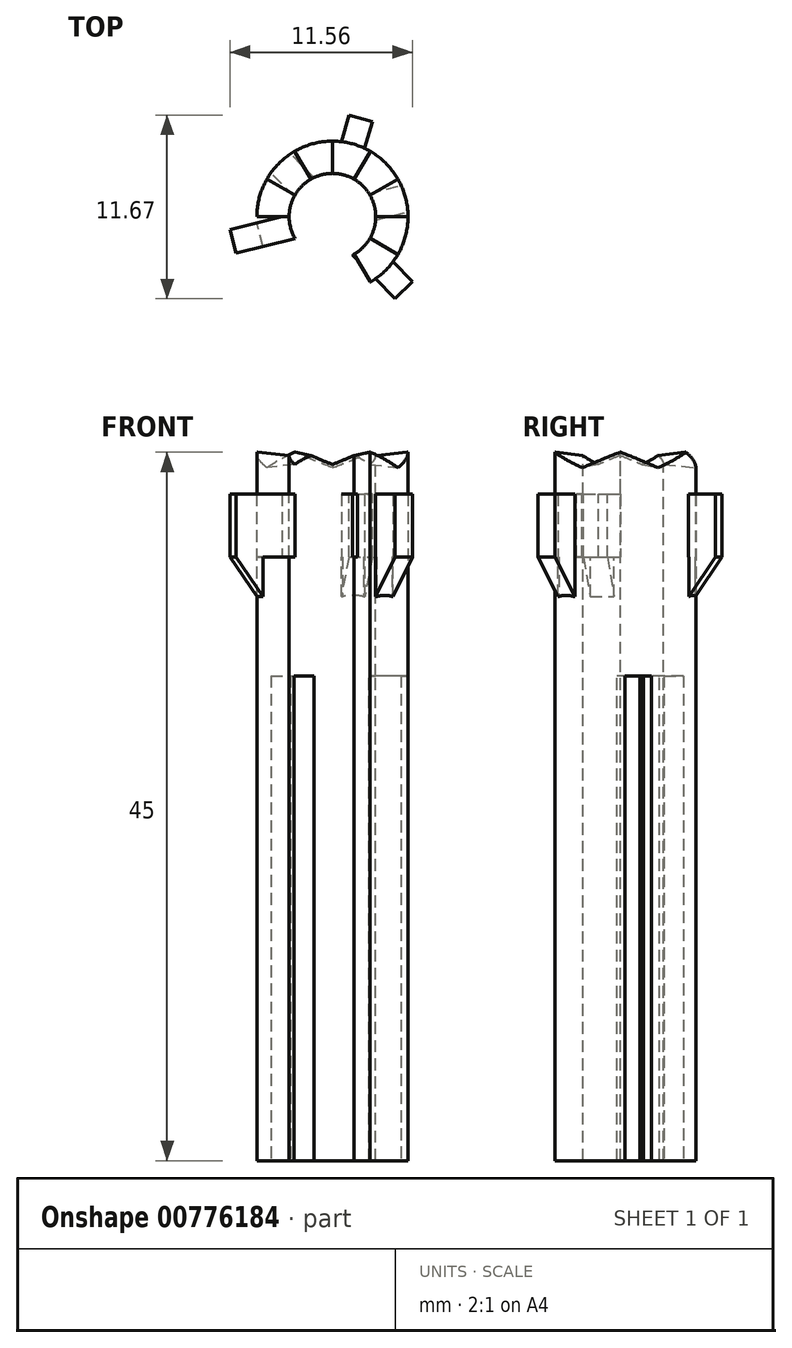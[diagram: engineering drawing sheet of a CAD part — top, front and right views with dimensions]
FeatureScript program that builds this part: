
annotation { "Feature Type Name" : "Feature", "Feature Type Description" : "" }
export const myFeature = defineFeature(function(context is Context, id is Id, definition is map)
    precondition{}
    {
        {
            var Q0;
            Q0=qCreatedBy(makeId("Front.planeOp"),FACE);
            var sketch = newSketch(context, id + "F0", { "sketchPlane" : qUnion([Q0])});
            skLineSegment(sketch, "E0.bottom", {"start": v(0, 0) * mm, "end": v(4.8, 0) * mm});
            skLineSegment(sketch, "E0.top", {"start": v(0, 45) * mm, "end": v(4.8, 45) * mm});
            skLineSegment(sketch, "E0.left", {"start": v(0, 0) * mm, "end": v(0, 45) * mm});
            skLineSegment(sketch, "E0.right", {"start": v(4.8, 0) * mm, "end": v(4.8, 45) * mm});
            skPoint(sketch, "E0.middle", {"position": v(2.4, 22.5) * mm});
            skSolve(sketch);
        }
        {
            var Q0;
            Q0=makeQuery(id+"F0.imprint","IMPRINT",FACE,{"disambiguationData":[TD([[makeQuery(id+"F0.imprint","IMPRINT",EDGE,{"derivedFrom":sQuery(id+"F0.wireOp",EDGE,"E0.bottom")}),1.0]])]});
            var Q1;
            Q1=sQuery(id+"F0.wireOp",EDGE,"E0.left");
            revolve(context, id + "F1", {"surfaceOperationType" : NewSurfaceOperationType.NEW, "entities" : qUnion([Q0]), "axis" : qUnion([Q1]), "revolveType" : RevolveType.ONE_DIRECTION, "angle" : 30 * degree});
        }
        {
            var Q0;
            Q0=sQuery(id+"F0.wireOp",EDGE,"E0.left");
            cPlane(context, id + "F2", {"entities" : qUnion([Q0]), "cplaneType" : CPlaneType.LINE_ANGLE, "offset" : 25 * mm, "angle" : 15 * degree, "width" : 150 * mm, "height" : 150 * mm});
        }
        {
            var Q0;
            Q0=qCreatedBy(id+"F2.planeOp",FACE);
            var sketch = newSketch(context, id + "F3", { "sketchPlane" : qUnion([Q0])});
            skLineSegment(sketch, "E1", {"start": v(0, 45.1) * mm, "end": v(1.34, 45.1) * mm});
            skLineSegment(sketch, "E2", {"start": v(1.34, 45.1) * mm, "end": v(1.34, 43.97) * mm});
            skLineSegment(sketch, "E3", {"start": v(1.34, 43.97) * mm, "end": v(-1.47, 45.1) * mm});
            skLineSegment(sketch, "E4", {"start": v(-1.47, 45.1) * mm, "end": v(0, 45.1) * mm});
            skSolve(sketch);
        }
        {
            var Q0;
            Q0=makeQuery(id+"F3.imprint","IMPRINT",FACE,{"disambiguationData":[TD([[makeQuery(id+"F3.imprint","IMPRINT",EDGE,{"derivedFrom":sQuery(id+"F3.wireOp",EDGE,"E1")}),-1.0]])]});
            extrude(context, id + "F4", {"entities" : qUnion([Q0]), "operationType" : NewBodyOperationType.REMOVE, "depth" : 5.8 * mm, "offsetDistance" : 25 * mm});
        }
        {
            var Q0;
            Q0=makeQuery(id+"F14.boolean.opBoolean","SPLIT",BODY,{"disambiguationData":[OD(0.0)],"derivedFrom":makeQuery(id+"F1.opRevolve","SWEPT_BODY",BODY,{"disambiguationData":[OSD([sQuery(id+"F0.wireOp",EDGE,"E0.bottom"),sQuery(id+"F0.wireOp",EDGE,"E0.top"),sQuery(id+"F0.wireOp",EDGE,"E0.left"),sQuery(id+"F0.wireOp",EDGE,"E0.right")])]})});
            var Q1;
            Q1=makeQuery(id+"F1.opRevolve","CAP_FACE",FACE,{"disambiguationData":[OSD([sQuery(id+"F0.wireOp",EDGE,"E0.bottom"),sQuery(id+"F0.wireOp",EDGE,"E0.top"),sQuery(id+"F0.wireOp",EDGE,"E0.left"),sQuery(id+"F0.wireOp",EDGE,"E0.right")])],"isStart":false});
            mirror(context, id + "F5", {"operationType" : NewBodyOperationType.ADD, "entities" : qUnion([Q0]), "mirrorPlane" : qUnion([Q1])});
        }
        {
            var Q0;
            Q0=makeQuery(id+"F14.boolean.opBoolean","SPLIT",BODY,{"disambiguationData":[OD(0.0)],"derivedFrom":makeQuery(id+"F1.opRevolve","SWEPT_BODY",BODY,{"disambiguationData":[OSD([sQuery(id+"F0.wireOp",EDGE,"E0.bottom"),sQuery(id+"F0.wireOp",EDGE,"E0.top"),sQuery(id+"F0.wireOp",EDGE,"E0.left"),sQuery(id+"F0.wireOp",EDGE,"E0.right")])]})});
            var Q1;
            Q1=makeQuery(id+"F5.opPattern","COPY",FACE,{"derivedFrom":makeQuery(id+"F1.opRevolve","CAP_FACE",FACE,{"disambiguationData":[OSD([sQuery(id+"F0.wireOp",EDGE,"E0.bottom"),sQuery(id+"F0.wireOp",EDGE,"E0.top"),sQuery(id+"F0.wireOp",EDGE,"E0.left"),sQuery(id+"F0.wireOp",EDGE,"E0.right")])],"isStart":true}),"instanceName":"1"});
            mirror(context, id + "F6", {"entities" : qUnion([Q0]), "mirrorPlane" : qUnion([Q1])});
        }
        {
            var Q0;
            Q0=makeQuery(id+"F6.opPattern","COPY",BODY,{"derivedFrom":makeQuery(id+"F14.boolean.opBoolean","SPLIT",BODY,{"disambiguationData":[OD(0.0)],"derivedFrom":makeQuery(id+"F1.opRevolve","SWEPT_BODY",BODY,{"disambiguationData":[OSD([sQuery(id+"F0.wireOp",EDGE,"E0.bottom"),sQuery(id+"F0.wireOp",EDGE,"E0.top"),sQuery(id+"F0.wireOp",EDGE,"E0.left"),sQuery(id+"F0.wireOp",EDGE,"E0.right")])]})}),"instanceName":"1"});
            var Q1;
            Q1=makeQuery(id+"F6.opPattern","COPY",FACE,{"derivedFrom":makeQuery(id+"F1.opRevolve","CAP_FACE",FACE,{"disambiguationData":[OSD([sQuery(id+"F0.wireOp",EDGE,"E0.bottom"),sQuery(id+"F0.wireOp",EDGE,"E0.top"),sQuery(id+"F0.wireOp",EDGE,"E0.left"),sQuery(id+"F0.wireOp",EDGE,"E0.right")])],"isStart":true}),"instanceName":"1"});
            mirror(context, id + "F7", {"entities" : qUnion([Q0]), "mirrorPlane" : qUnion([Q1])});
        }
        {
            var Q0;
            Q0=makeQuery(id+"F14.boolean.opBoolean","SPLIT",BODY,{"disambiguationData":[OD(0.0)],"derivedFrom":makeQuery(id+"F1.opRevolve","SWEPT_BODY",BODY,{"disambiguationData":[OSD([sQuery(id+"F0.wireOp",EDGE,"E0.bottom"),sQuery(id+"F0.wireOp",EDGE,"E0.top"),sQuery(id+"F0.wireOp",EDGE,"E0.left"),sQuery(id+"F0.wireOp",EDGE,"E0.right")])]})});
            var Q1;
            Q1=makeQuery(id+"F7.opPattern","COPY",FACE,{"derivedFrom":makeQuery(id+"F6.opPattern","COPY",FACE,{"derivedFrom":makeQuery(id+"F5.opPattern","COPY",FACE,{"derivedFrom":makeQuery(id+"F1.opRevolve","CAP_FACE",FACE,{"disambiguationData":[OSD([sQuery(id+"F0.wireOp",EDGE,"E0.bottom"),sQuery(id+"F0.wireOp",EDGE,"E0.top"),sQuery(id+"F0.wireOp",EDGE,"E0.left"),sQuery(id+"F0.wireOp",EDGE,"E0.right")])],"isStart":true}),"instanceName":"1"}),"instanceName":"1"}),"instanceName":"1"});
            mirror(context, id + "F8", {"operationType" : NewBodyOperationType.ADD, "entities" : qUnion([Q0]), "mirrorPlane" : qUnion([Q1])});
        }
        {
            var Q0;
            Q0=qCreatedBy(makeId("Right.planeOp"),FACE);
            var sketch = newSketch(context, id + "F9", { "sketchPlane" : qUnion([Q0])});
            skLineSegment(sketch, "E5.bottom", {"start": v(0, 0) * mm, "end": v(2.75, 0) * mm});
            skLineSegment(sketch, "E5.top", {"start": v(0, 45) * mm, "end": v(2.75, 45) * mm});
            skLineSegment(sketch, "E5.left", {"start": v(0, 0) * mm, "end": v(0, 45) * mm});
            skLineSegment(sketch, "E5.right", {"start": v(2.75, 0) * mm, "end": v(2.75, 45) * mm});
            skPoint(sketch, "E5.middle", {"position": v(1.37, 22.5) * mm});
            skSolve(sketch);
        }
        {
            var Q0;
            Q0=sQuery(id+"F0.wireOp",EDGE,"E0.left");
            cPlane(context, id + "F10", {"entities" : qUnion([Q0]), "cplaneType" : CPlaneType.LINE_ANGLE, "offset" : 25 * mm, "angle" : 74 * degree, "width" : 150 * mm, "height" : 150 * mm});
        }
        {
            var Q0;
            Q0=qCreatedBy(id+"F10.planeOp",FACE);
            var sketch = newSketch(context, id + "F11", { "sketchPlane" : qUnion([Q0])});
            skLineSegment(sketch, "E6.bottom", {"start": v(0.78, 38.33) * mm, "end": v(-0.78, 38.33) * mm});
            skLineSegment(sketch, "E6.top", {"start": v(0.78, 42.33) * mm, "end": v(-0.78, 42.33) * mm});
            skLineSegment(sketch, "E6.left", {"start": v(0.78, 38.33) * mm, "end": v(0.78, 42.33) * mm});
            skLineSegment(sketch, "E6.right", {"start": v(-0.78, 38.33) * mm, "end": v(-0.77, 42.33) * mm});
            skPoint(sketch, "E6.middle", {"position": v(0, 40.33) * mm});
            skLineSegment(sketch, "E7", {"start": v(0, 38.33) * mm, "end": v(0, 30.8) * mm});
            skSolve(sketch);
        }
        {
            var Q0;
            Q0=makeQuery(id+"F11.imprint","IMPRINT",FACE,{"disambiguationData":[TD([[makeQuery(id+"F11.imprint","IMPRINT",EDGE,{"derivedFrom":sQuery(id+"F11.wireOp",EDGE,"E6.bottom")}),-1.0]])]});
            extrude(context, id + "F12", {"entities" : qUnion([Q0]), "depth" : 6.5 * mm, "offsetDistance" : 25 * mm});
        }
        {
            var Q0;
            Q0=makeQuery(id+"F12.opExtrude","SWEPT_BODY",BODY,{"disambiguationData":[OSD([sQuery(id+"F11.wireOp",EDGE,"E6.bottom"),sQuery(id+"F11.wireOp",EDGE,"E6.top"),sQuery(id+"F11.wireOp",EDGE,"E6.left"),sQuery(id+"F11.wireOp",EDGE,"E6.right")])]});
            var Q1;
            Q1=sQuery(id+"F0.wireOp",EDGE,"E0.left");
            circularPattern(context, id + "F13", {"operationType" : NewBodyOperationType.ADD, "entities" : qUnion([Q0]), "axis" : qUnion([Q1]), "angle" : 360 * degree, "instanceCount" : 3, "equalSpace" : true});
        }
        {
            var Q0;
            Q0 = qSketchRegion(id + "F9", true);
            var Q1;
            Q1=sQuery(id+"F9.wireOp",EDGE,"E5.left");
            revolve(context, id + "F14", {"operationType" : NewBodyOperationType.REMOVE, "surfaceOperationType" : NewSurfaceOperationType.NEW, "entities" : qUnion([Q0]), "axis" : qUnion([Q1]), "revolveType" : RevolveType.FULL, "oppositeDirection" : true});
        }
        {
            var Q0;
            Q0=qCreatedBy(id+"F10.planeOp",FACE);
            var sketch = newSketch(context, id + "F15", { "sketchPlane" : qUnion([Q0])});
            skLineSegment(sketch, "E8.bottom", {"start": v(-0.88, 30.8) * mm, "end": v(0.87, 30.8) * mm});
            skLineSegment(sketch, "E8.top", {"start": v(-0.88, -0.67) * mm, "end": v(0.87, -0.67) * mm});
            skLineSegment(sketch, "E8.left", {"start": v(-0.88, 30.8) * mm, "end": v(-0.88, -0.67) * mm});
            skLineSegment(sketch, "E8.right", {"start": v(0.87, 30.8) * mm, "end": v(0.87, -0.67) * mm});
            skPoint(sketch, "E8.middle", {"position": v(0, 15.06) * mm});
            skSolve(sketch);
        }
        {
            var Q0;
            Q0=makeQuery(id+"F15.imprint","IMPRINT",FACE,{"disambiguationData":[TD([[makeQuery(id+"F15.imprint","IMPRINT",EDGE,{"derivedFrom":sQuery(id+"F15.wireOp",EDGE,"E8.bottom")}),-1.0]])]});
            extrude(context, id + "F16", {"entities" : qUnion([Q0]), "oppositeDirection" : true, "depth" : 6 * mm, "offsetDistance" : 25 * mm});
        }
        {
            var Q0;
            Q0=makeQuery(id+"F16.opExtrude","SWEPT_BODY",BODY,{"disambiguationData":[OSD([sQuery(id+"F15.wireOp",EDGE,"E8.bottom"),sQuery(id+"F15.wireOp",EDGE,"E8.top"),sQuery(id+"F15.wireOp",EDGE,"E8.left"),sQuery(id+"F15.wireOp",EDGE,"E8.right")])]});
            var Q1;
            Q1=sQuery(id+"F11.wireOp",EDGE,"E7");
            circularPattern(context, id + "F17", {"operationType" : NewBodyOperationType.REMOVE, "entities" : qUnion([Q0]), "axis" : qUnion([Q1]), "angle" : 360 * degree, "instanceCount" : 3, "equalSpace" : true});
        }
        {
            var Q0;
            Q0=sQuery(id+"F0.wireOp",EDGE,"E0.left");
            cPlane(context, id + "F18", {"entities" : qUnion([Q0]), "cplaneType" : CPlaneType.LINE_ANGLE, "offset" : 25 * mm, "angle" : 44 * degree, "width" : 150 * mm, "height" : 150 * mm});
        }
        {
            var Q0;
            Q0=qCreatedBy(id+"F18.planeOp",FACE);
            var sketch = newSketch(context, id + "F19", { "sketchPlane" : qUnion([Q0])});
            skLineSegment(sketch, "E9", {"start": v(-6.5, 38.33) * mm, "end": v(-4.75, 35.83) * mm});
            skLineSegment(sketch, "E10", {"start": v(-4.75, 35.83) * mm, "end": v(-4.75, 38.33) * mm});
            skLineSegment(sketch, "E11", {"start": v(-4.75, 38.33) * mm, "end": v(-6.5, 38.33) * mm});
            skSolve(sketch);
        }
        {
            var Q0;
            Q0=makeQuery(id+"F19.imprint","IMPRINT",FACE,{"disambiguationData":[TD([[makeQuery(id+"F19.imprint","IMPRINT",EDGE,{"derivedFrom":sQuery(id+"F19.wireOp",EDGE,"E9")}),1.0]])]});
            extrude(context, id + "F20", {"entities" : qUnion([Q0]), "endBound" : BoundingType.SYMMETRIC, "depth" : 1.55 * mm, "offsetDistance" : 25 * mm});
        }
        {
            var Q0;
            Q0=makeQuery(id+"F20.opExtrude","SWEPT_BODY",BODY,{"disambiguationData":[OSD([sQuery(id+"F19.wireOp",EDGE,"E9"),sQuery(id+"F19.wireOp",EDGE,"E10"),sQuery(id+"F19.wireOp",EDGE,"E11")])]});
            var Q1;
            Q1=sQuery(id+"F0.wireOp",EDGE,"E0.left");
            circularPattern(context, id + "F21", {"operationType" : NewBodyOperationType.ADD, "entities" : qUnion([Q0]), "axis" : qUnion([Q1]), "angle" : 360 * degree, "instanceCount" : 3, "equalSpace" : true});
        }
    });
